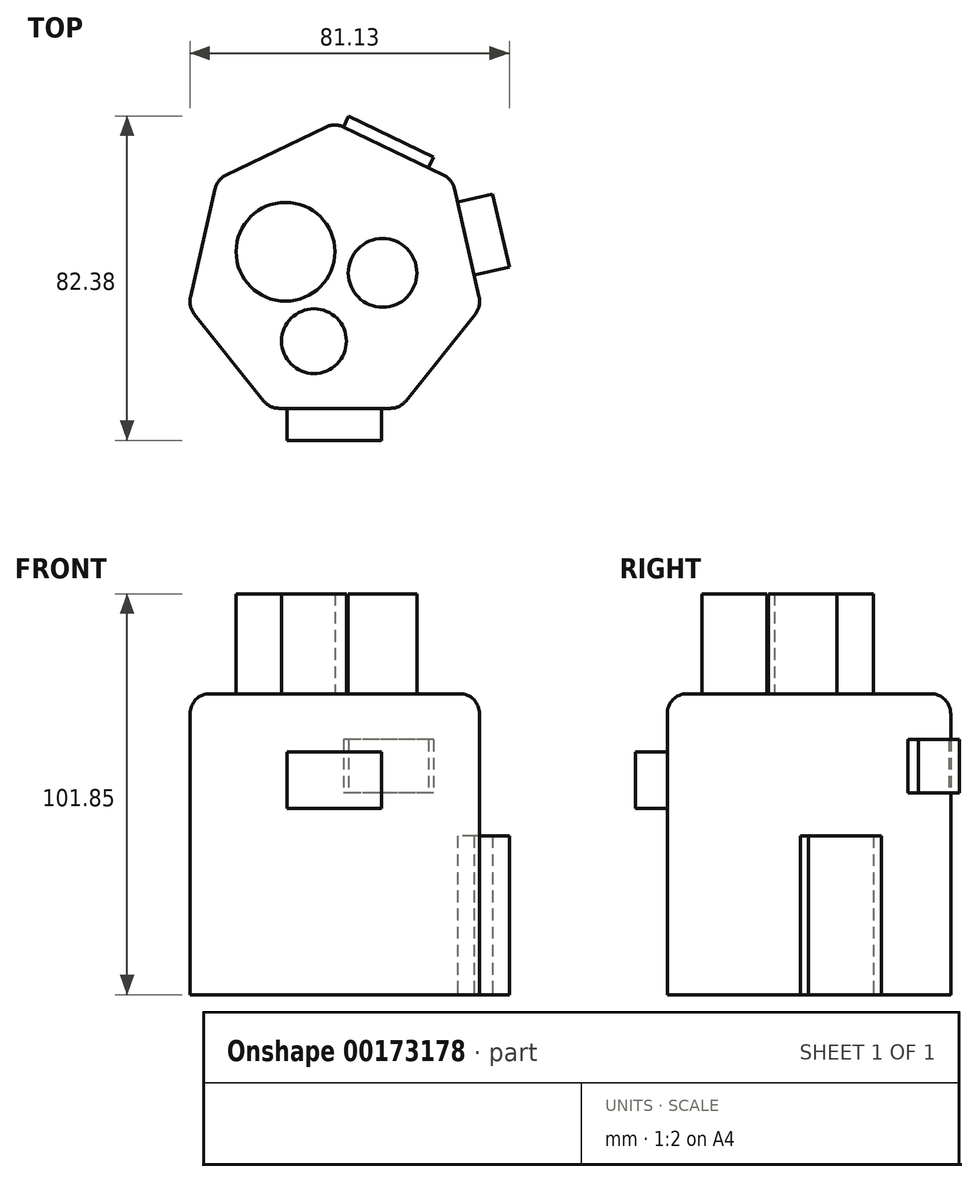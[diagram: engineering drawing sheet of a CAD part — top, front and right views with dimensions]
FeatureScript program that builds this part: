
annotation { "Feature Type Name" : "Feature", "Feature Type Description" : "" }
export const myFeature = defineFeature(function(context is Context, id is Id, definition is map)
    precondition{}
    {
        {
            var Q0;
            Q0=qCreatedBy(makeId("Top.planeOp"),FACE);
            var sketch = newSketch(context, id + "F0", { "sketchPlane" : qUnion([Q0])});
            skCircle(sketch, "E0.cCircle", {"center": v(0, 0) * mm, "radius": 34.4 * mm, "construction": true});
            skLineSegment(sketch, "E0.0", {"start": v(16.56, -34.4) * mm, "end": v(-16.56, -34.4) * mm});
            skLineSegment(sketch, "E0.1", {"start": v(-16.56, -34.4) * mm, "end": v(-37.22, -8.5) * mm});
            skLineSegment(sketch, "E0.2", {"start": v(-37.22, -8.5) * mm, "end": v(-29.85, 23.8) * mm});
            skLineSegment(sketch, "E0.3", {"start": v(-29.85, 23.8) * mm, "end": v(0, 38.17) * mm});
            skLineSegment(sketch, "E0.4", {"start": v(0, 38.17) * mm, "end": v(29.85, 23.8) * mm});
            skLineSegment(sketch, "E0.5", {"start": v(29.85, 23.8) * mm, "end": v(37.22, -8.5) * mm});
            skLineSegment(sketch, "E0.6", {"start": v(37.22, -8.5) * mm, "end": v(16.56, -34.4) * mm});
            skPoint(sketch, "E0.0.midPoint", {"position": v(0, -34.4) * mm});
            skSolve(sketch);
        }
        {
            var Q0;
            Q0=makeQuery(id+"F0.imprint","IMPRINT",FACE,{"disambiguationData":[TD([[makeQuery(id+"F0.imprint","IMPRINT",EDGE,{"derivedFrom":sQuery(id+"F0.wireOp",EDGE,"E0.0")}),-1.0]])]});
            extrude(context, id + "F1", {"entities" : qUnion([Q0]), "depth" : 76.45 * mm});
        }
        {
            var Q0;
            Q0=makeQuery(id+"F1.opExtrude","CAP_EDGE",EDGE,{"disambiguationData":[OSD([sQuery(id+"F0.wireOp",EDGE,"E0.5")])],"isStart":false});
            var Q1;
            Q1=makeQuery(id+"F1.opExtrude","CAP_EDGE",EDGE,{"disambiguationData":[OSD([sQuery(id+"F0.wireOp",EDGE,"E0.4")])],"isStart":false});
            var Q2;
            Q2=makeQuery(id+"F1.opExtrude","CAP_EDGE",EDGE,{"disambiguationData":[OSD([sQuery(id+"F0.wireOp",EDGE,"E0.3")])],"isStart":false});
            var Q3;
            Q3=makeQuery(id+"F1.opExtrude","CAP_EDGE",EDGE,{"disambiguationData":[OSD([sQuery(id+"F0.wireOp",EDGE,"E0.2")])],"isStart":false});
            var Q4;
            Q4=makeQuery(id+"F1.opExtrude","CAP_EDGE",EDGE,{"disambiguationData":[OSD([sQuery(id+"F0.wireOp",EDGE,"E0.1")])],"isStart":false});
            var Q5;
            Q5=makeQuery(id+"F1.opExtrude","CAP_EDGE",EDGE,{"disambiguationData":[OSD([sQuery(id+"F0.wireOp",EDGE,"E0.0")])],"isStart":false});
            var Q6;
            Q6=makeQuery(id+"F1.opExtrude","CAP_FACE",FACE,{"disambiguationData":[OSD([sQuery(id+"F0.wireOp",EDGE,"E0.0"),sQuery(id+"F0.wireOp",EDGE,"E0.1"),sQuery(id+"F0.wireOp",EDGE,"E0.2"),sQuery(id+"F0.wireOp",EDGE,"E0.3"),sQuery(id+"F0.wireOp",EDGE,"E0.4"),sQuery(id+"F0.wireOp",EDGE,"E0.5"),sQuery(id+"F0.wireOp",EDGE,"E0.6")])],"isStart":false});
            var Q7;
            Q7=makeQuery(id+"F1.opExtrude","SWEPT_EDGE",EDGE,{"disambiguationData":[OSD([sQuery(id+"F0.wireOp",EDGE,"E0.4"),sQuery(id+"F0.wireOp",EDGE,"E0.5")])]});
            var Q8;
            Q8=makeQuery(id+"F1.opExtrude","SWEPT_EDGE",EDGE,{"disambiguationData":[OSD([sQuery(id+"F0.wireOp",EDGE,"E0.3"),sQuery(id+"F0.wireOp",EDGE,"E0.4")])]});
            var Q9;
            Q9=makeQuery(id+"F1.opExtrude","SWEPT_EDGE",EDGE,{"disambiguationData":[OSD([sQuery(id+"F0.wireOp",EDGE,"E0.5"),sQuery(id+"F0.wireOp",EDGE,"E0.6")])]});
            var Q10;
            Q10=makeQuery(id+"F1.opExtrude","SWEPT_EDGE",EDGE,{"disambiguationData":[OSD([sQuery(id+"F0.wireOp",EDGE,"E0.0"),sQuery(id+"F0.wireOp",EDGE,"E0.6")])]});
            var Q11;
            Q11=makeQuery(id+"F1.opExtrude","SWEPT_EDGE",EDGE,{"disambiguationData":[OSD([sQuery(id+"F0.wireOp",EDGE,"E0.2"),sQuery(id+"F0.wireOp",EDGE,"E0.3")])]});
            var Q12;
            Q12=makeQuery(id+"F1.opExtrude","SWEPT_EDGE",EDGE,{"disambiguationData":[OSD([sQuery(id+"F0.wireOp",EDGE,"E0.1"),sQuery(id+"F0.wireOp",EDGE,"E0.2")])]});
            var Q13;
            Q13=makeQuery(id+"F1.opExtrude","SWEPT_EDGE",EDGE,{"disambiguationData":[OSD([sQuery(id+"F0.wireOp",EDGE,"E0.0"),sQuery(id+"F0.wireOp",EDGE,"E0.1")])]});
            fillet(context, id + "F2", {"entities" : qUnion([Q0, Q1, Q2, Q3, Q4, Q5, Q6, Q7, Q8, Q9, Q10, Q11, Q12, Q13]), "radius" : 5.08 * mm, "tangentPropagation" : true, "allowEdgeOverflow" : false});
        }
        {
            var Q0;
            Q0=makeQuery(id+"F1.opExtrude","CAP_FACE",FACE,{"disambiguationData":[OSD([sQuery(id+"F0.wireOp",EDGE,"E0.0"),sQuery(id+"F0.wireOp",EDGE,"E0.1"),sQuery(id+"F0.wireOp",EDGE,"E0.2"),sQuery(id+"F0.wireOp",EDGE,"E0.3"),sQuery(id+"F0.wireOp",EDGE,"E0.4"),sQuery(id+"F0.wireOp",EDGE,"E0.5"),sQuery(id+"F0.wireOp",EDGE,"E0.6")])],"isStart":false});
            var sketch = newSketch(context, id + "F3", { "sketchPlane" : qUnion([Q0])});
            skCircle(sketch, "E1", {"center": v(-12.54, 5.39) * mm, "radius": 12.54 * mm});
            skCircle(sketch, "E2", {"center": v(12.14, 0) * mm, "radius": 8.72 * mm});
            skCircle(sketch, "E3", {"center": v(-5.29, -17.33) * mm, "radius": 8.23 * mm});
            skSolve(sketch);
        }
        {
            var Q0;
            Q0=makeQuery(id+"F3.imprint","IMPRINT",FACE,{"disambiguationData":[TD([[makeQuery(id+"F3.imprint","IMPRINT",EDGE,{"derivedFrom":sQuery(id+"F3.wireOp",EDGE,"E1")}),1.0]])]});
            var Q1;
            Q1=makeQuery(id+"F3.imprint","IMPRINT",FACE,{"disambiguationData":[TD([[makeQuery(id+"F3.imprint","IMPRINT",EDGE,{"derivedFrom":sQuery(id+"F3.wireOp",EDGE,"E2")}),1.0]])]});
            var Q2;
            Q2=makeQuery(id+"F3.imprint","IMPRINT",FACE,{"disambiguationData":[TD([[makeQuery(id+"F3.imprint","IMPRINT",EDGE,{"derivedFrom":sQuery(id+"F3.wireOp",EDGE,"E3")}),1.0]])]});
            extrude(context, id + "F4", {"entities" : qUnion([Q0, Q1, Q2]), "operationType" : NewBodyOperationType.ADD, "depth" : 25.4 * mm});
        }
        {
            var Q0;
            Q0=makeQuery(id+"F1.opExtrude","SWEPT_FACE",FACE,{"disambiguationData":[OSD([sQuery(id+"F0.wireOp",EDGE,"E0.5")])]});
            var sketch = newSketch(context, id + "F5", { "sketchPlane" : qUnion([Q0])});
            skLineSegment(sketch, "E4.bottom", {"start": v(-8.46, 40.28) * mm, "end": v(10.6, 40.28) * mm});
            skLineSegment(sketch, "E4.top", {"start": v(-8.46, 0) * mm, "end": v(10.6, 0) * mm});
            skLineSegment(sketch, "E4.left", {"start": v(-8.46, 40.28) * mm, "end": v(-8.46, 0) * mm});
            skLineSegment(sketch, "E4.right", {"start": v(10.6, 40.28) * mm, "end": v(10.6, 0) * mm});
            skSolve(sketch);
        }
        {
            var Q0;
            Q0=makeQuery(id+"F5.imprint","IMPRINT",FACE,{"disambiguationData":[TD([[makeQuery(id+"F5.imprint","IMPRINT",EDGE,{"derivedFrom":sQuery(id+"F5.wireOp",EDGE,"E4.bottom")}),-1.0]])]});
            extrude(context, id + "F6", {"entities" : qUnion([Q0]), "operationType" : NewBodyOperationType.ADD, "depth" : 9.14 * mm});
        }
        {
            var Q0;
            Q0=makeQuery(id+"F1.opExtrude","SWEPT_FACE",FACE,{"disambiguationData":[OSD([sQuery(id+"F0.wireOp",EDGE,"E0.4")])]});
            var sketch = newSketch(context, id + "F7", { "sketchPlane" : qUnion([Q0])});
            skLineSegment(sketch, "E5.bottom", {"start": v(-9.85, 64.8) * mm, "end": v(14.12, 64.8) * mm});
            skLineSegment(sketch, "E5.top", {"start": v(-9.85, 51.31) * mm, "end": v(14.12, 51.31) * mm});
            skLineSegment(sketch, "E5.left", {"start": v(-9.85, 64.8) * mm, "end": v(-9.85, 51.31) * mm});
            skLineSegment(sketch, "E5.right", {"start": v(14.12, 64.8) * mm, "end": v(14.12, 51.31) * mm});
            skSolve(sketch);
        }
        {
            var Q0;
            Q0=makeQuery(id+"F7.imprint","IMPRINT",FACE,{"disambiguationData":[TD([[makeQuery(id+"F7.imprint","IMPRINT",EDGE,{"derivedFrom":sQuery(id+"F7.wireOp",EDGE,"E5.bottom")}),-1.0]])]});
            extrude(context, id + "F8", {"entities" : qUnion([Q0]), "operationType" : NewBodyOperationType.ADD, "depth" : 3.05 * mm});
        }
        {
            var Q0;
            Q0=makeQuery(id+"F6.opExtrude","CAP_FACE",FACE,{"disambiguationData":[OSD([sQuery(id+"F5.wireOp",EDGE,"E4.bottom"),sQuery(id+"F5.wireOp",EDGE,"E4.top"),sQuery(id+"F5.wireOp",EDGE,"E4.left"),sQuery(id+"F5.wireOp",EDGE,"E4.right")])],"isStart":false});
            var sketch = newSketch(context, id + "F9", { "sketchPlane" : qUnion([Q0])});
            skCircle(sketch, "E6", {"center": v(3.91, 19.35) * mm, "radius": 2.3 * mm});
            skSolve(sketch);
        }
        {
            var Q0;
            Q0 = qSketchRegion(id + "F9", true);
            extrude(context, id + "F10", {"entities" : qUnion([Q0]), "operationType" : NewBodyOperationType.ADD, "oppositeDirection" : true, "depth" : 5.33 * mm});
        }
        {
            var Q0;
            Q0=makeQuery(id+"F1.opExtrude","SWEPT_FACE",FACE,{"disambiguationData":[OSD([sQuery(id+"F0.wireOp",EDGE,"E0.0")])]});
            var sketch = newSketch(context, id + "F11", { "sketchPlane" : qUnion([Q0])});
            skLineSegment(sketch, "E7.bottom", {"start": v(-12.13, 61.68) * mm, "end": v(11.9, 61.68) * mm});
            skLineSegment(sketch, "E7.top", {"start": v(-12.13, 47.27) * mm, "end": v(11.9, 47.27) * mm});
            skLineSegment(sketch, "E7.left", {"start": v(-12.13, 61.68) * mm, "end": v(-12.13, 47.27) * mm});
            skLineSegment(sketch, "E7.right", {"start": v(11.9, 61.68) * mm, "end": v(11.9, 47.27) * mm});
            skSolve(sketch);
        }
        {
            var Q0;
            Q0=makeQuery(id+"F11.imprint","IMPRINT",FACE,{"disambiguationData":[TD([[makeQuery(id+"F11.imprint","IMPRINT",EDGE,{"derivedFrom":sQuery(id+"F11.wireOp",EDGE,"E7.bottom")}),-1.0]])]});
            extrude(context, id + "F12", {"entities" : qUnion([Q0]), "operationType" : NewBodyOperationType.ADD, "depth" : 8.13 * mm});
        }
    });
